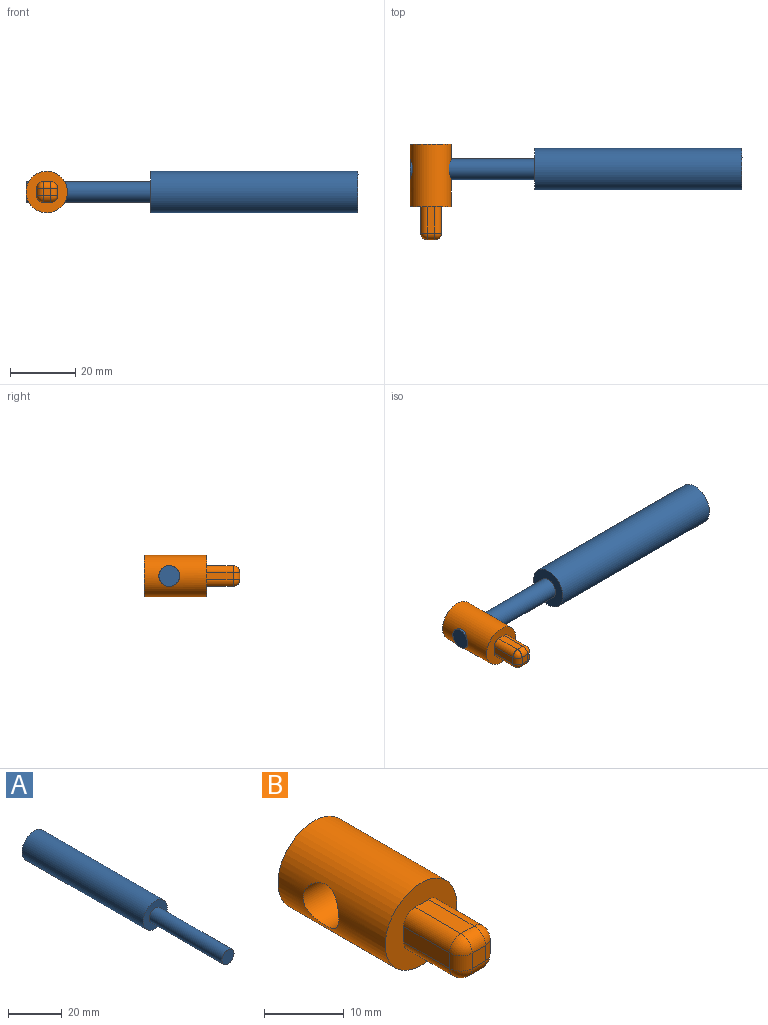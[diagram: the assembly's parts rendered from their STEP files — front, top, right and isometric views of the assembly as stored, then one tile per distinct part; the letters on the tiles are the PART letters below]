
ASSEMBLY  parts=2 mates=1
PART A: 5 faces, bbox 12.7x101.6x12.7 mm
  f0: cylinder r=6.35mm len=63.5mm, axis (0,1,0), area 2533.5mm2, adj f1,f2
  f1: plane 12.7x12.7mm, normal (0,-1,0), area 95mm2, adj f0,f3
  f2: plane 12.7x12.7mm, normal (0,1,0), area 126.7mm2, adj f0
  f3: cylinder r=3.17mm len=38.1mm, axis (0,1,0), area 760.1mm2, adj f1,f4
  f4: plane 6.35x6.35mm, normal (0,-1,0), area 31.7mm2, adj f3
PART B: 21 faces, bbox 12.7x29.2x12.7 mm
  f0: cylinder r=6.35mm len=19.05mm, axis (0,1,0), area 694.5mm2, adj f1,f2,f20
  f1: plane 12.7x12.7mm, normal (0,-1,0), area 89.8mm2, adj f0,f3,f4,f5,f6,f8,f9,f10
  f2: plane 12.7x12.7mm, normal (0,1,0), area 126.7mm2, adj f0
  f3: plane 8.16x2.35mm, normal (0,0,1), area 19.2mm2, adj f1,f10,f11,f18
  f4: plane 8.16x2.35mm, normal (-1,0,0), area 19.2mm2, adj f1,f8,f11,f14
  f5: plane 8.16x2.35mm, normal (0,0,-1), area 19.2mm2, adj f1,f8,f9,f13
  f6: plane 8.16x2.35mm, normal (1,0,0), area 19.2mm2, adj f1,f9,f10,f17
  f7: plane 2.35x2.35mm, normal (0,-1,0), area 5.5mm2, adj f13,f14,f17,f18
  f8: cylinder r=2mm len=8.16mm, axis (0,1,0), area 25.6mm2, adj f1,f4,f5,f12
  f9: cylinder r=2mm len=8.16mm, axis (0,-1,0), area 25.6mm2, adj f1,f5,f6,f15
  f10: cylinder r=2mm len=8.16mm, axis (0,1,0), area 25.6mm2, adj f1,f3,f6,f19
  f11: cylinder r=2mm len=8.16mm, axis (0,-1,0), area 25.6mm2, adj f1,f3,f4,f16
  f12: sphere r=2mm, area 6.3mm2, adj f8,f13,f14
  f13: cylinder r=2mm len=2.35mm, axis (-1,0,0), area 7.4mm2, adj f5,f7,f12,f15
  f14: cylinder r=2mm len=2.35mm, axis (0,0,1), area 7.4mm2, adj f4,f7,f12,f16
  f15: sphere r=2mm, area 6.3mm2, adj f9,f13,f17
  f16: sphere r=2mm, area 6.3mm2, adj f11,f14,f18
  f17: cylinder r=2mm len=2.35mm, axis (0,0,-1), area 7.4mm2, adj f6,f7,f15,f19
  f18: cylinder r=2mm len=2.35mm, axis (1,0,0), area 7.4mm2, adj f3,f7,f16,f19
  f19: sphere r=2mm, area 6.3mm2, adj f10,f17,f18
  f20: cylinder r=3.17mm len=12.7mm, axis (1,0,0), area 236.7mm2, adj f0
PLACE A rot(axis=(0.58,0.58,-0.58),120deg) t=(21.29,150.9,-39.38)mm
PLACE B t=(-8.4,113.69,-24.9)mm
MATE slider A.f0 <-> B.f20  axis (1,0,0) through (-61.26,106.07,20.75)mm
